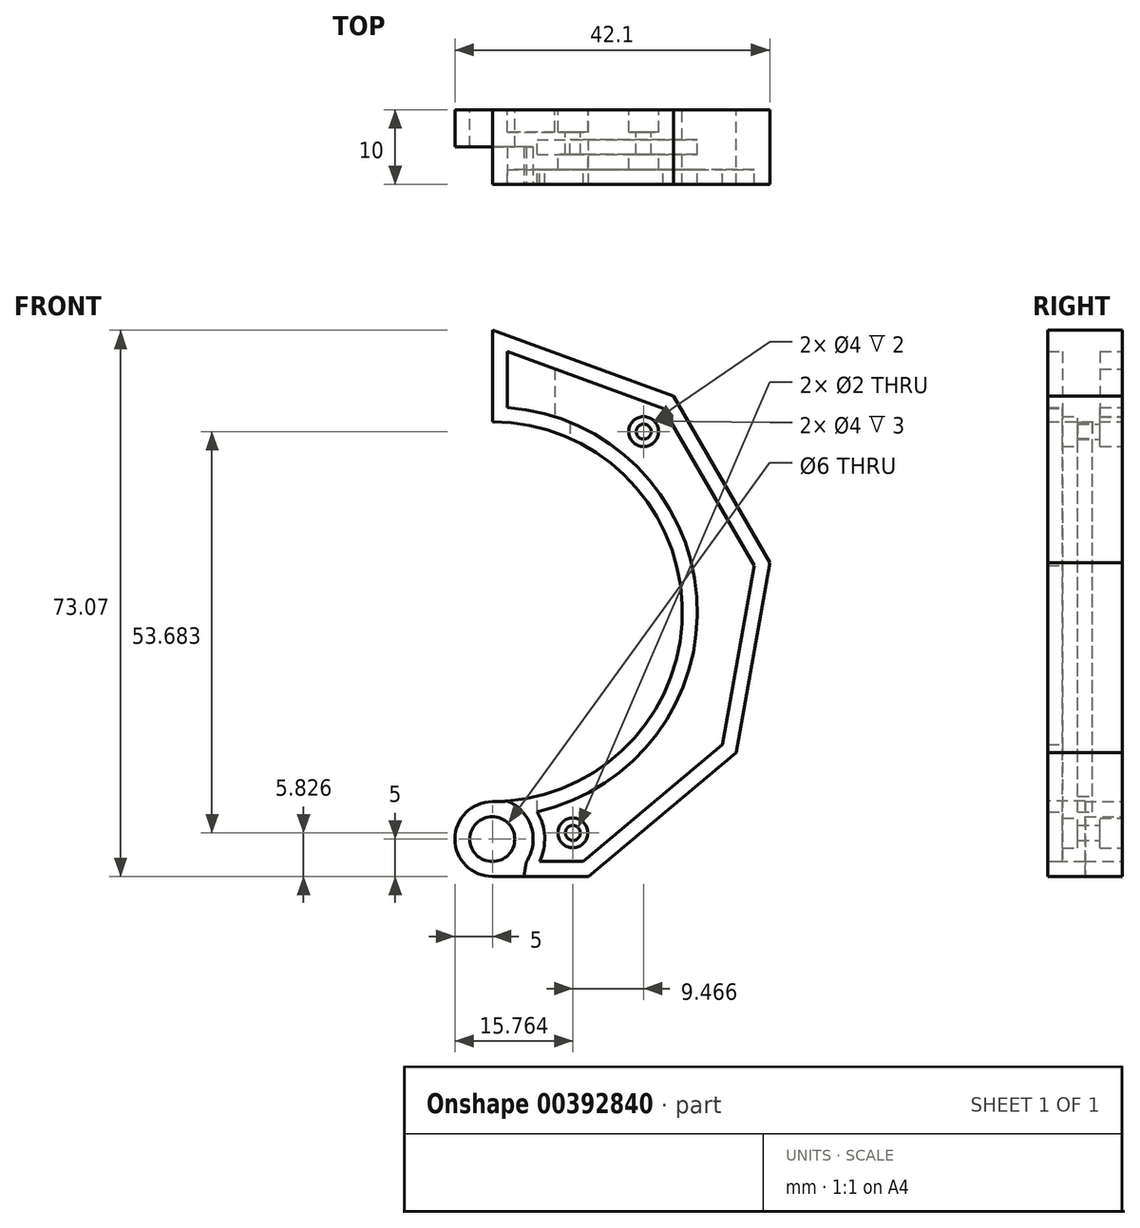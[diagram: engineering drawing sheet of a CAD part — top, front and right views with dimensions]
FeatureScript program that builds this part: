
annotation { "Feature Type Name" : "Feature", "Feature Type Description" : "" }
export const myFeature = defineFeature(function(context is Context, id is Id, definition is map)
    precondition{}
    {
        {
            var Q0;
            Q0=qCreatedBy(makeId("Front.planeOp"),FACE);
            var sketch = newSketch(context, id + "F0", { "sketchPlane" : qUnion([Q0])});
            skLineSegment(sketch, "E0.0", {"start": v(12.88, -35.4) * mm, "end": v(0, -35.4) * mm});
            skLineSegment(sketch, "E0.5", {"start": v(0, 37.67) * mm, "end": v(24.22, 28.86) * mm});
            skLineSegment(sketch, "E0.6", {"start": v(24.22, 28.86) * mm, "end": v(37.1, 6.54) * mm});
            skLineSegment(sketch, "E0.7", {"start": v(37.1, 6.54) * mm, "end": v(32.62, -18.84) * mm});
            skLineSegment(sketch, "E0.8", {"start": v(32.62, -18.84) * mm, "end": v(12.88, -35.4) * mm});
            skPoint(sketch, "E0.0.midPoint", {"position": v(0, -35.4) * mm});
            skLineSegment(sketch, "E1.0", {"start": v(12.16, -33.4) * mm, "end": v(6.32, -33.4) * mm});
            skLineSegment(sketch, "E1.5", {"start": v(2, 34.82) * mm, "end": v(22.85, 27.23) * mm});
            skLineSegment(sketch, "E1.6", {"start": v(22.85, 27.23) * mm, "end": v(35, 6.17) * mm});
            skLineSegment(sketch, "E1.7", {"start": v(35, 6.17) * mm, "end": v(30.78, -17.77) * mm});
            skLineSegment(sketch, "E1.8", {"start": v(30.78, -17.77) * mm, "end": v(12.16, -33.4) * mm});
            skPoint(sketch, "E1.0.midPoint", {"position": v(0, -33.4) * mm});
            skArc(sketch, "E2", {"start": v(0, -25.4) * mm, "mid": v(25.4, 0) * mm, "end": v(0, 25.4) * mm});
            skArc(sketch, "E3", {"start": v(5, -30.4) * mm, "mid": v(-3.54, -26.86) * mm, "end": v(0, -35.4) * mm});
            skCircle(sketch, "E4", {"center": v(0, -30.4) * mm, "radius": 3 * mm});
            skLineSegment(sketch, "E5", {"start": v(0, 25.4) * mm, "end": v(0, 37.67) * mm});
            skArc(sketch, "E6.trimOffspring", {"start": v(6.32, -33.4) * mm, "mid": v(6.99, -30.03) * mm, "end": v(5.97, -26.74) * mm});
            skArc(sketch, "E7.trimOffspring", {"start": v(5.97, -26.74) * mm, "mid": v(27.33, 2) * mm, "end": v(2, 27.33) * mm});
            skLineSegment(sketch, "E8", {"start": v(2, 34.82) * mm, "end": v(2, 27.33) * mm});
            skPoint(sketch, "E9.orphan", {"position": v(0, -27.4) * mm});
            skLineSegment(sketch, "E10", {"start": v(5.97, -26.74) * mm, "end": v(5.97, -24.69) * mm});
            skLineSegment(sketch, "E11", {"start": v(10.36, 25.36) * mm, "end": v(10.36, 23.19) * mm});
            skCircle(sketch, "E12", {"center": v(20.23, 24.1) * mm, "radius": 2 * mm});
            skCircle(sketch, "E13", {"center": v(20.23, 24.1) * mm, "radius": 1 * mm});
            skCircle(sketch, "E14", {"center": v(31, 5.47) * mm, "radius": 2 * mm});
            skCircle(sketch, "E15", {"center": v(27.26, -15.74) * mm, "radius": 2 * mm});
            skPoint(sketch, "E16.centerSnap0", {"position": v(6.99, -30.03) * mm});
            skArc(sketch, "E17", {"start": v(5, -30.4) * mm, "mid": v(4.38, -33.16) * mm, "end": v(2.65, -35.4) * mm});
            skCircle(sketch, "E18", {"center": v(10.76, -29.57) * mm, "radius": 2 * mm});
            skCircle(sketch, "E19", {"center": v(10.76, -29.57) * mm, "radius": 1 * mm});
            skSolve(sketch);
        }
        {
            var Q0;
            Q0=makeQuery(id+"F0.imprint","IMPRINT",FACE,{"disambiguationData":[TD([[makeQuery(id+"F0.imprint","IMPRINT",EDGE,{"derivedFrom":sQuery(id+"F0.wireOp",EDGE,"E4")}),-1.0]])]});
            extrude(context, id + "F1", {"entities" : qUnion([Q0]), "depth" : 5 * mm});
        }
        {
            var Q0;
            Q0=makeQuery(id+"F0.imprint","IMPRINT",FACE,{"disambiguationData":[TD([[makeQuery(id+"F0.imprint","IMPRINT",EDGE,{"derivedFrom":sQuery(id+"F0.wireOp",EDGE,"E0.5")}),-1.0]])]});
            extrude(context, id + "F2", {"entities" : qUnion([Q0]), "operationType" : NewBodyOperationType.ADD, "depth" : 10 * mm});
        }
        {
            var Q0;
            Q0=makeQuery(id+"F0.imprint","IMPRINT",FACE,{"disambiguationData":[TD([[makeQuery(id+"F0.imprint","IMPRINT",EDGE,{"derivedFrom":sQuery(id+"F0.wireOp",EDGE,"E1.0")}),-1.0]])]});
            var Q1;
            Q1=makeQuery(id+"F0.imprint","IMPRINT",FACE,{"disambiguationData":[TD([[makeQuery(id+"F0.imprint","IMPRINT",EDGE,{"derivedFrom":sQuery(id+"F0.wireOp",EDGE,"E14")}),1.0]])]});
            var Q2;
            Q2=makeQuery(id+"F0.imprint","IMPRINT",FACE,{"disambiguationData":[TD([[makeQuery(id+"F0.imprint","IMPRINT",EDGE,{"derivedFrom":sQuery(id+"F0.wireOp",EDGE,"E15")}),1.0]])]});
            extrude(context, id + "F3", {"entities" : qUnion([Q0, Q1, Q2]), "operationType" : NewBodyOperationType.ADD, "depth" : 8 * mm});
        }
        {
            var Q0;
            {var subQ0=sQuery(id+"F0.wireOp",EDGE,"E10");Q0=makeQuery(id+"F0.imprint","IMPRINT",FACE,{"disambiguationData":[TD([[makeQuery(id+"F0.imprint","IMPRINT",EDGE,{"derivedFrom":subQ0}),-1.0]])]});}
            extrude(context, id + "F4", {"entities" : qUnion([Q0]), "operationType" : NewBodyOperationType.ADD, "depth" : 4 * mm});
        }
        {
            var Q0;
            Q0=makeQuery(id+"F2.opExtrude","CAP_FACE",FACE,{"disambiguationData":[OSD([sQuery(id+"F0.wireOp",EDGE,"E0.0"),sQuery(id+"F0.wireOp",EDGE,"E0.5"),sQuery(id+"F0.wireOp",EDGE,"E0.6"),sQuery(id+"F0.wireOp",EDGE,"E0.7"),sQuery(id+"F0.wireOp",EDGE,"E0.8"),sQuery(id+"F0.wireOp",EDGE,"E1.0"),sQuery(id+"F0.wireOp",EDGE,"E1.5"),sQuery(id+"F0.wireOp",EDGE,"E1.6"),sQuery(id+"F0.wireOp",EDGE,"E1.7"),sQuery(id+"F0.wireOp",EDGE,"E1.8"),sQuery(id+"F0.wireOp",EDGE,"E2"),sQuery(id+"F0.wireOp",EDGE,"E3"),sQuery(id+"F0.wireOp",EDGE,"E5"),sQuery(id+"F0.wireOp",EDGE,"E6.trimOffspring"),sQuery(id+"F0.wireOp",EDGE,"E7.trimOffspring"),sQuery(id+"F0.wireOp",EDGE,"E8"),sQuery(id+"F0.wireOp",EDGE,"E10"),sQuery(id+"F0.wireOp",EDGE,"E11"),sQuery(id+"F0.wireOp",EDGE,"E17")])],"isStart":false});
            var sketch = newSketch(context, id + "F5", { "sketchPlane" : qUnion([Q0])});
            skLineSegment(sketch, "E20.0.0", {"start": v(5.97, -24.69) * mm, "end": v(5.97, -26.74) * mm});
            skArc(sketch, "E20.0.1", {"start": v(5.97, -26.74) * mm, "mid": v(27.3, -2.3) * mm, "end": v(10.36, 25.36) * mm});
            skLineSegment(sketch, "E20.0.2", {"start": v(10.36, 25.36) * mm, "end": v(10.36, 23.19) * mm});
            skArc(sketch, "E20.0.3", {"start": v(10.36, 23.19) * mm, "mid": v(25.3, -2.32) * mm, "end": v(5.97, -24.69) * mm});
            skSolve(sketch);
        }
        {
            var Q0;
            Q0=makeQuery(id+"F5.imprint","IMPRINT",FACE,{"disambiguationData":[TD([[makeQuery(id+"F5.imprint","IMPRINT",EDGE,{"derivedFrom":sQuery(id+"F5.wireOp",EDGE,"E20.0.0")}),-1.0]])]});
            extrude(context, id + "F6", {"entities" : qUnion([Q0]), "operationType" : NewBodyOperationType.ADD, "oppositeDirection" : true, "depth" : 4 * mm});
        }
        {
            var Q0;
            Q0=makeQuery(id+"F0.imprint","IMPRINT",FACE,{"disambiguationData":[TD([[makeQuery(id+"F0.imprint","IMPRINT",EDGE,{"derivedFrom":sQuery(id+"F0.wireOp",EDGE,"E12")}),1.0]])]});
            var Q1;
            Q1=makeQuery(id+"F0.imprint","IMPRINT",FACE,{"disambiguationData":[TD([[makeQuery(id+"F0.imprint","IMPRINT",EDGE,{"derivedFrom":sQuery(id+"F0.wireOp",EDGE,"E18")}),1.0]])]});
            extrude(context, id + "F7", {"entities" : qUnion([Q0, Q1]), "operationType" : NewBodyOperationType.ADD, "depth" : 6 * mm});
        }
        {
            var Q0;
            Q0=makeQuery(id+"F6.boolean.opBoolean","MERGE",FACE,{"derivedFrom":[makeQuery(id+"F2.opExtrude","CAP_FACE",FACE,{"disambiguationData":[OSD([sQuery(id+"F0.wireOp",EDGE,"E0.0"),sQuery(id+"F0.wireOp",EDGE,"E0.5"),sQuery(id+"F0.wireOp",EDGE,"E0.6"),sQuery(id+"F0.wireOp",EDGE,"E0.7"),sQuery(id+"F0.wireOp",EDGE,"E0.8"),sQuery(id+"F0.wireOp",EDGE,"E1.0"),sQuery(id+"F0.wireOp",EDGE,"E1.5"),sQuery(id+"F0.wireOp",EDGE,"E1.6"),sQuery(id+"F0.wireOp",EDGE,"E1.7"),sQuery(id+"F0.wireOp",EDGE,"E1.8"),sQuery(id+"F0.wireOp",EDGE,"E2"),sQuery(id+"F0.wireOp",EDGE,"E3"),sQuery(id+"F0.wireOp",EDGE,"E5"),sQuery(id+"F0.wireOp",EDGE,"E6.trimOffspring"),sQuery(id+"F0.wireOp",EDGE,"E7.trimOffspring"),sQuery(id+"F0.wireOp",EDGE,"E8"),sQuery(id+"F0.wireOp",EDGE,"E10"),sQuery(id+"F0.wireOp",EDGE,"E11"),sQuery(id+"F0.wireOp",EDGE,"E17")])],"isStart":false}),makeQuery(id+"F6.opExtrude","CAP_FACE",FACE,{"disambiguationData":[OSD([sQuery(id+"F5.wireOp",EDGE,"E20.0.0"),sQuery(id+"F5.wireOp",EDGE,"E20.0.1"),sQuery(id+"F5.wireOp",EDGE,"E20.0.2"),sQuery(id+"F5.wireOp",EDGE,"E20.0.3")])],"isStart":true})]});
            var sketch = newSketch(context, id + "F8", { "sketchPlane" : qUnion([Q0])});
            skLineSegment(sketch, "E21", {"start": v(4.65, -32.5) * mm, "end": v(4.65, -32.5) * mm});
            skLineSegment(sketch, "E22", {"start": v(4.2, -35.4) * mm, "end": v(4.54, -33.42) * mm});
            skArc(sketch, "E23", {"start": v(4.54, -33.42) * mm, "mid": v(4.8, -27.82) * mm, "end": v(0, -24.94) * mm});
            skArc(sketch, "E24", {"start": v(0, -25.4) * mm, "mid": v(5, -30.4) * mm, "end": v(0, -35.4) * mm});
            skLineSegment(sketch, "E25", {"start": v(4.2, -35.4) * mm, "end": v(0, -35.4) * mm});
            skLineSegment(sketch, "E26", {"start": v(0, -24.94) * mm, "end": v(0, -25.4) * mm});
            skSolve(sketch);
        }
        {
            var Q0;
            Q0 = qSketchRegion(id + "F8", true);
            extrude(context, id + "F9", {"entities" : qUnion([Q0]), "operationType" : NewBodyOperationType.REMOVE, "oppositeDirection" : true, "depth" : 5 * mm});
        }
        {
            var Q0;
            Q0=makeQuery(id+"F0.imprint","IMPRINT",FACE,{"disambiguationData":[TD([[makeQuery(id+"F0.imprint","IMPRINT",EDGE,{"derivedFrom":sQuery(id+"F0.wireOp",EDGE,"E12")}),1.0]])]});
            var Q1;
            Q1=makeQuery(id+"F0.imprint","IMPRINT",FACE,{"disambiguationData":[TD([[makeQuery(id+"F0.imprint","IMPRINT",EDGE,{"derivedFrom":sQuery(id+"F0.wireOp",EDGE,"E18")}),1.0]])]});
            extrude(context, id + "F10", {"entities" : qUnion([Q0, Q1]), "operationType" : NewBodyOperationType.REMOVE, "depth" : 3 * mm});
        }
        {
            var Q0;
            Q0=makeQuery(id+"F0.imprint","IMPRINT",FACE,{"disambiguationData":[TD([[makeQuery(id+"F0.imprint","IMPRINT",EDGE,{"derivedFrom":sQuery(id+"F0.wireOp",EDGE,"E1.0")}),-1.0]])]});
            var sketch = newSketch(context, id + "F11", { "sketchPlane" : qUnion([Q0])});
            skLineSegment(sketch, "E27.5", {"start": v(2, 34.82) * mm, "end": v(8.36, 32.5) * mm});
            skLineSegment(sketch, "E28", {"start": v(0, 25.4) * mm, "end": v(0, 37.67) * mm});
            skArc(sketch, "E29.trimOffspring", {"start": v(8.36, 26.1) * mm, "mid": v(5.22, 26.9) * mm, "end": v(2, 27.33) * mm});
            skLineSegment(sketch, "E30", {"start": v(2, 34.82) * mm, "end": v(2, 27.33) * mm});
            skLineSegment(sketch, "E31", {"start": v(10.36, 25.36) * mm, "end": v(10.36, 23.19) * mm});
            skLineSegment(sketch, "E32", {"start": v(10.36, 25.36) * mm, "end": v(10.36, 33.9) * mm});
            skArc(sketch, "E33.trimOffspring", {"start": v(10.36, 23.19) * mm, "mid": v(5.3, 24.84) * mm, "end": v(0, 25.4) * mm});
            skLineSegment(sketch, "E34", {"start": v(8.36, 32.5) * mm, "end": v(8.36, 26.1) * mm});
            skPoint(sketch, "E35.start.orphan", {"position": v(3.76, 36.3) * mm});
            skLineSegment(sketch, "E36.trimOffspring", {"start": v(7.52, 34.94) * mm, "end": v(10.36, 33.9) * mm});
            skLineSegment(sketch, "E37", {"start": v(0, 37.67) * mm, "end": v(7.52, 34.94) * mm});
            skPoint(sketch, "E38.0", {"position": v(0, 25.4) * mm});
            skSolve(sketch);
        }
        {
            var Q0;
            Q0=makeQuery(id+"F11.imprint","IMPRINT",FACE,{"disambiguationData":[TD([[makeQuery(id+"F11.imprint","IMPRINT",EDGE,{"derivedFrom":sQuery(id+"F11.wireOp",EDGE,"E27.5")}),-1.0]])]});
            extrude(context, id + "F12", {"entities" : qUnion([Q0]), "operationType" : NewBodyOperationType.REMOVE, "depth" : 3 * mm});
        }
    });
